# Revit family: E_Actuator_F_MEPcontent_Oventrop_Aktor T ST
name_source: partatom
category: Electrical Fixtures
revit_build: Autodesk Revit MEP 2015 (Build: 20140606_1530(x64)
units: mm (PartAtom-declared; Revit-internal decimal feet)

## types (1)
- 2953
    Ambient Temperature = 0 °C up to 60 °C
    Article Description = Electrothermal actuator "Aktor T ST" "L NC", 24 V, closed with current "off", 0-10 V
    Article Type = 2953
    Black = Color RGB 060-060-060
    Cap Length = 6.2 mm  [stored 0.0203412 ft]
    Cap Length 2 = 8.5 mm  [stored 0.0278871 ft]
    Connecting Cable = 3 x 0.22 mm², length 1 m, plug-in connection
    Content Supplier URL = www.mepcontent.eu
    Continuous Current = about 42 mA
    Control Voltage = 0-10 V DC
    Custom = No
    Default Elevation = 1219.2 mm  [stored 4 ft]
    Description = Electrothermal actuator "Aktor T ST" "L NC", 24 V, closed with current "off", 0-10 V
    EMCS Version = 2.0
    ETIM Article Class = EC011290
    Family Version = 10.14
    Fluid Temperature = 0 °C up to 100 °C
    GTIN = 4026755423365
    Grey = Color RGB 100-100-100
    Height = 53 mm  [stored 0.173885 ft]
    IFCExportAs = IfcActuatorType
    IFCExportType = ELECTRICACTUATOR
    Input Impedance = 100 kW
    Length = 61.5 mm  [stored 0.201772 ft]
    MEPcontent Class = ACTUATOR
    Manufacturer = Oventrop
    Manufacturer Art. No. = 1012953
    Manufacturer URL = https://www.oventrop.com
    Medium Floating Time = 30 s/mm
    Model = 2953
    Operating Power = > 90 N
    Piston Stroke = automatic recognition
    Product Line = Oventrop
    Protection = IP 54 in any position
    Protective System = III according to EN 60730
    Revit Version = 2015
    Start Up Load = < 320 mA for a max. of 2 min.
    Storage Temperature = -25 °C up to +60 °C
    Travel = 5.0 mm
    URL = www.stabiplan.com
    Voltage = 24 V
    White = Color RGB 245-245-245
    Width = 44.3 mm  [stored 0.145341 ft]

note: [stored X ft] marks values corroborated as IEEE doubles in the binary element streams (Revit-internal decimal feet)

## geometry (parser evidence)
native form markers: Sweep x2
no freeform markers — native parametric forms only
